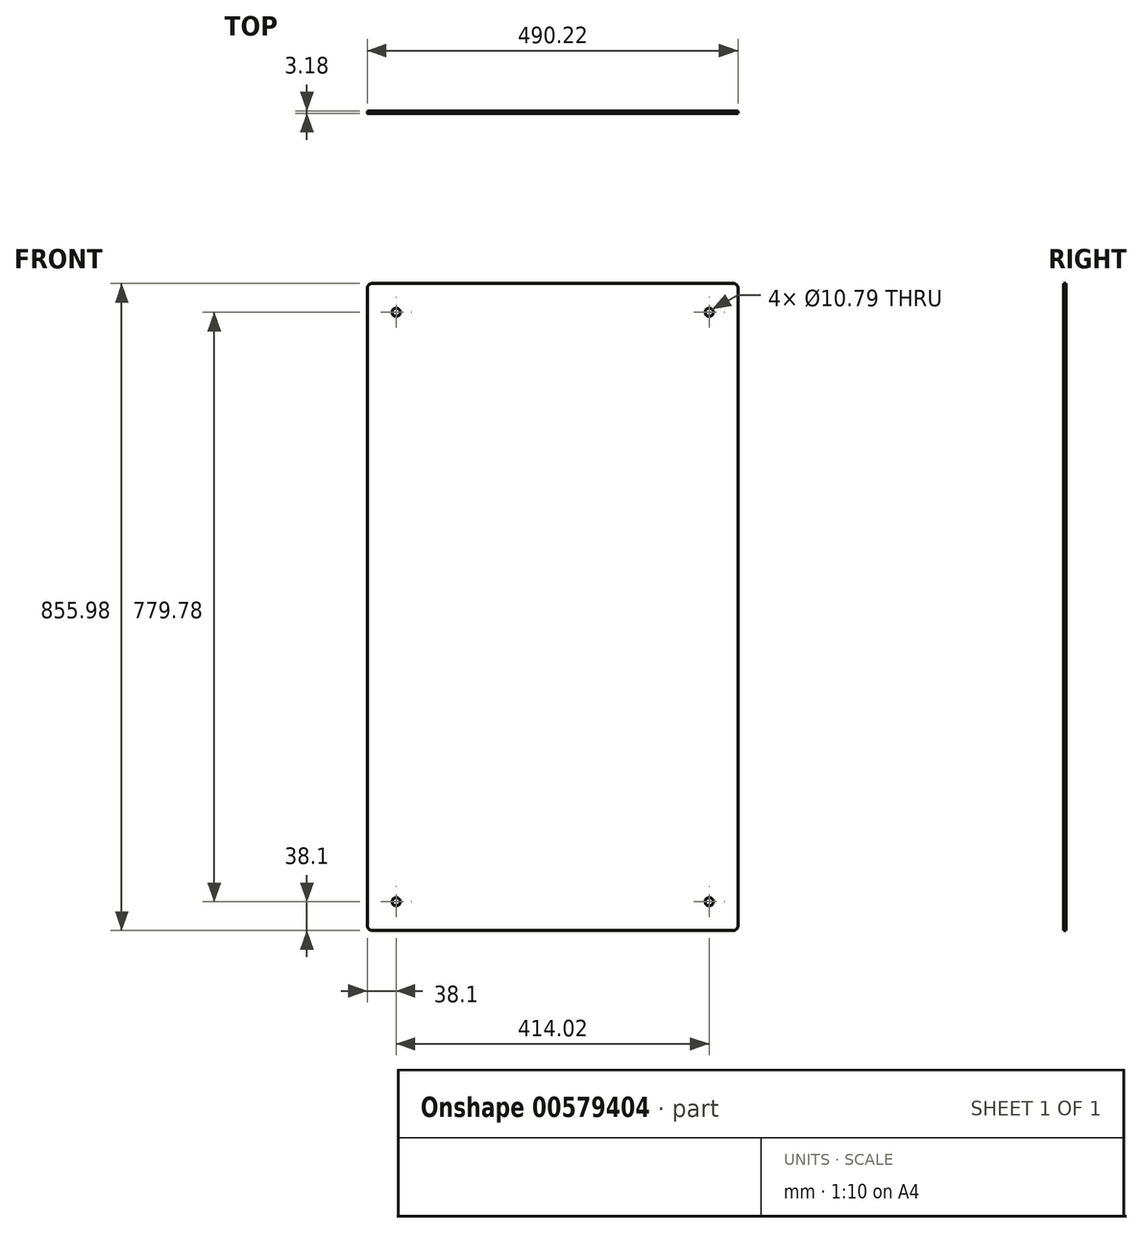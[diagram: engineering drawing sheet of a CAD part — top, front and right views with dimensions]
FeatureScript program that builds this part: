
annotation { "Feature Type Name" : "Feature", "Feature Type Description" : "" }
export const myFeature = defineFeature(function(context is Context, id is Id, definition is map)
    precondition{}
    {
        {
            var Q0;
            Q0=qCreatedBy(makeId("Front.planeOp"),FACE);
            var sketch = newSketch(context, id + "F0", { "sketchPlane" : qUnion([Q0])});
            skLineSegment(sketch, "E0.bottom", {"start": v(238.76, -428) * mm, "end": v(-238.76, -428) * mm});
            skLineSegment(sketch, "E0.top", {"start": v(238.76, 428) * mm, "end": v(-238.76, 428) * mm});
            skLineSegment(sketch, "E0.left", {"start": v(245.11, -421.64) * mm, "end": v(245.11, 421.64) * mm});
            skLineSegment(sketch, "E0.right", {"start": v(-245.11, -421.64) * mm, "end": v(-245.11, 421.64) * mm});
            skPoint(sketch, "E0.middle", {"position": v(0, 0) * mm});
            skLineSegment(sketch, "E1.bottom", {"start": v(207.01, -389.9) * mm, "end": v(-207.01, -389.9) * mm, "construction": true});
            skLineSegment(sketch, "E1.top", {"start": v(207, 389.9) * mm, "end": v(-207.01, 389.9) * mm, "construction": true});
            skLineSegment(sketch, "E1.left", {"start": v(207.01, -389.9) * mm, "end": v(207.01, 389.9) * mm, "construction": true});
            skLineSegment(sketch, "E1.right", {"start": v(-207.01, -389.9) * mm, "end": v(-207.01, 389.9) * mm, "construction": true});
            skCircle(sketch, "E2", {"center": v(-207.01, 389.9) * mm, "radius": 5.4 * mm});
            skCircle(sketch, "E3", {"center": v(207.01, 389.9) * mm, "radius": 5.4 * mm});
            skCircle(sketch, "E4", {"center": v(207.01, -389.9) * mm, "radius": 5.4 * mm});
            skCircle(sketch, "E5", {"center": v(-207.01, -389.9) * mm, "radius": 5.4 * mm});
            skPoint(sketch, "E6.visualSharp", {"position": v(-245.11, 428) * mm});
            skArc(sketch, "E6.filletArc", {"start": v(-238.76, 428) * mm, "mid": v(-243.25, 426.13) * mm, "end": v(-245.11, 421.64) * mm});
            skPoint(sketch, "E7.visualSharp", {"position": v(245.11, 428) * mm});
            skArc(sketch, "E7.filletArc", {"start": v(245.11, 421.64) * mm, "mid": v(243.25, 426.13) * mm, "end": v(238.76, 428) * mm});
            skPoint(sketch, "E8.visualSharp", {"position": v(245.11, -428) * mm});
            skArc(sketch, "E8.filletArc", {"start": v(238.76, -428) * mm, "mid": v(243.25, -426.13) * mm, "end": v(245.11, -421.64) * mm});
            skPoint(sketch, "E9.visualSharp", {"position": v(-245.11, -428) * mm});
            skArc(sketch, "E9.filletArc", {"start": v(-245.11, -421.64) * mm, "mid": v(-243.25, -426.13) * mm, "end": v(-238.76, -428) * mm});
            skSolve(sketch);
        }
        {
            var Q0;
            Q0=makeQuery(id+"F0.imprint","IMPRINT",FACE,{"disambiguationData":[TD([[makeQuery(id+"F0.imprint","IMPRINT",EDGE,{"derivedFrom":sQuery(id+"F0.wireOp",EDGE,"E0.bottom")}),-1.0]])]});
            extrude(context, id + "F1", {"entities" : qUnion([Q0]), "depth" : 3.17 * mm, "offsetDistance" : 25.4 * mm});
        }
    });
